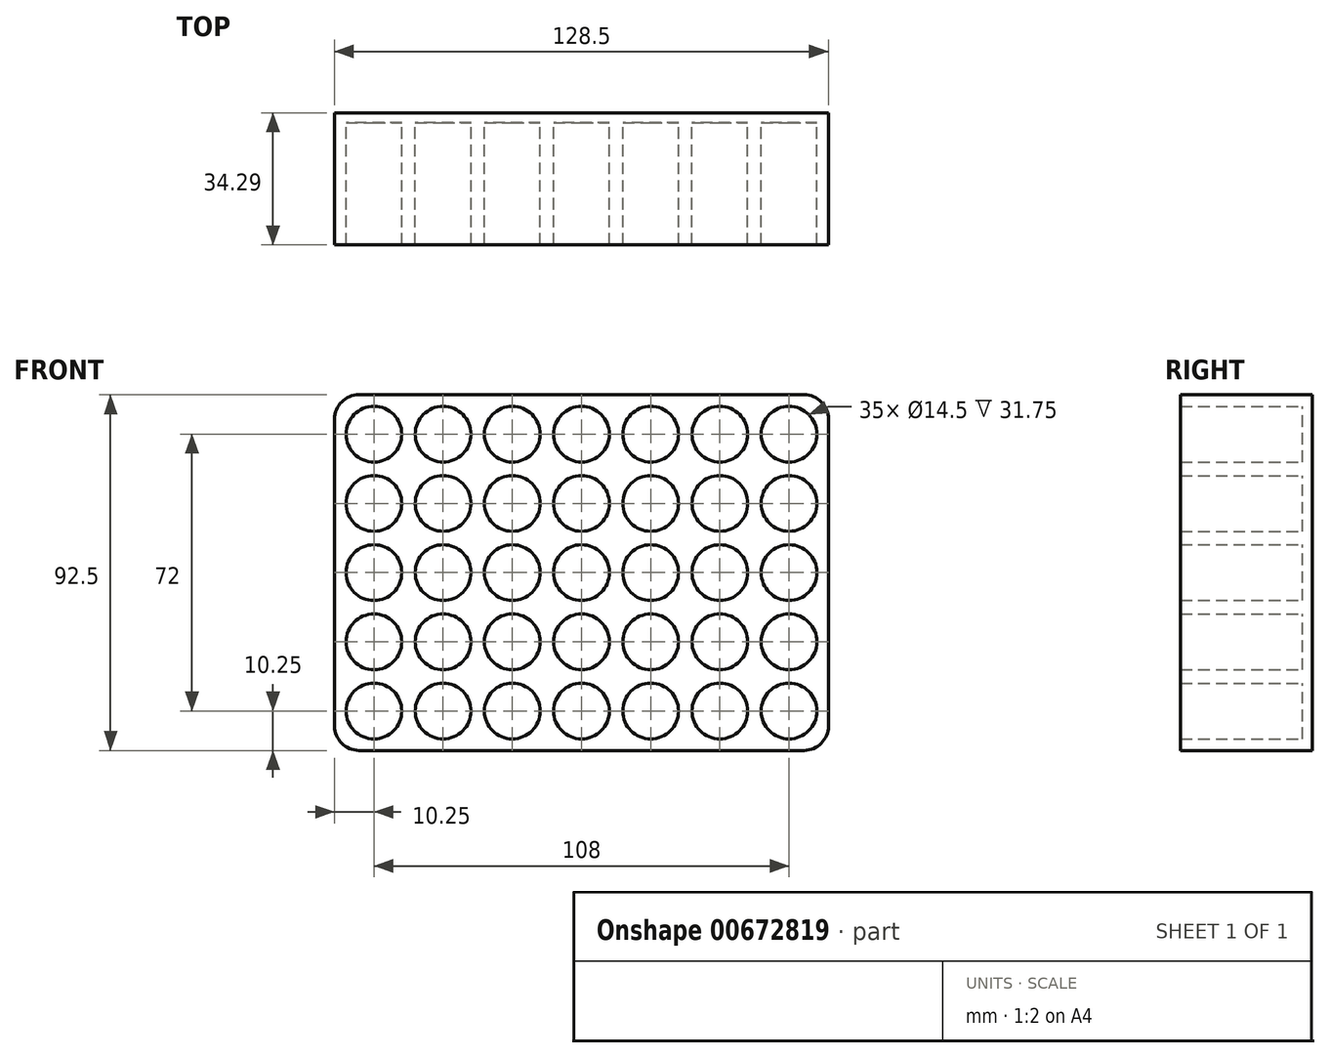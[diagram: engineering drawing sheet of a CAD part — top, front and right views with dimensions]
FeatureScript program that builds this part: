
annotation { "Feature Type Name" : "Feature", "Feature Type Description" : "" }
export const myFeature = defineFeature(function(context is Context, id is Id, definition is map)
    precondition{}
    {
        {
            var Q0;
            Q0=qCreatedBy(makeId("Front.planeOp"),FACE);
            var sketch = newSketch(context, id + "F0", { "sketchPlane" : qUnion([Q0])});
            skLineSegment(sketch, "E0.bottom", {"start": v(57.9, -46.25) * mm, "end": v(-57.9, -46.25) * mm});
            skLineSegment(sketch, "E0.top", {"start": v(57.9, 46.25) * mm, "end": v(-57.9, 46.25) * mm});
            skLineSegment(sketch, "E0.left", {"start": v(64.25, -39.9) * mm, "end": v(64.25, 39.9) * mm});
            skLineSegment(sketch, "E0.right", {"start": v(-64.25, -39.9) * mm, "end": v(-64.25, 39.9) * mm});
            skPoint(sketch, "E0.middle", {"position": v(0, 0) * mm});
            skCircle(sketch, "E1", {"center": v(0, 0) * mm, "radius": 7.25 * mm});
            skCircle(sketch, "E2.1.0.0", {"center": v(18, 0) * mm, "radius": 7.25 * mm});
            skCircle(sketch, "E2.2.0.0", {"center": v(36, 0) * mm, "radius": 7.25 * mm});
            skCircle(sketch, "E2.3.0.0", {"center": v(54, 0) * mm, "radius": 7.25 * mm});
            skLineSegment(sketch, "E2.direction1", {"start": v(0, 0) * mm, "end": v(18, 0) * mm, "construction": true});
            skCircle(sketch, "E3.1.0.0", {"center": v(-18, 0) * mm, "radius": 7.25 * mm});
            skCircle(sketch, "E3.2.0.0", {"center": v(-36, 0) * mm, "radius": 7.25 * mm});
            skCircle(sketch, "E3.3.0.0", {"center": v(-54, 0) * mm, "radius": 7.25 * mm});
            skLineSegment(sketch, "E3.direction1", {"start": v(0, 0) * mm, "end": v(-18, 0) * mm, "construction": true});
            skCircle(sketch, "E4", {"center": v(-54, 18) * mm, "radius": 7.25 * mm});
            skCircle(sketch, "E5", {"center": v(-54, -18) * mm, "radius": 7.25 * mm});
            skCircle(sketch, "E6", {"center": v(-36, -18) * mm, "radius": 7.25 * mm});
            skCircle(sketch, "E7", {"center": v(-36, 18) * mm, "radius": 7.25 * mm});
            skCircle(sketch, "E8", {"center": v(-18, 18) * mm, "radius": 7.25 * mm});
            skCircle(sketch, "E9", {"center": v(-18, -18) * mm, "radius": 7.25 * mm});
            skCircle(sketch, "E10", {"center": v(0, 18) * mm, "radius": 7.25 * mm});
            skCircle(sketch, "E11", {"center": v(0, -18) * mm, "radius": 7.25 * mm});
            skCircle(sketch, "E12", {"center": v(18, -18) * mm, "radius": 7.25 * mm});
            skCircle(sketch, "E13", {"center": v(36, -18) * mm, "radius": 7.25 * mm});
            skCircle(sketch, "E14", {"center": v(18, 18) * mm, "radius": 7.25 * mm});
            skCircle(sketch, "E15", {"center": v(36, 18) * mm, "radius": 7.25 * mm});
            skCircle(sketch, "E16", {"center": v(54, 18) * mm, "radius": 7.25 * mm});
            skCircle(sketch, "E17", {"center": v(54, -18) * mm, "radius": 7.25 * mm});
            skCircle(sketch, "E18", {"center": v(-54, -36) * mm, "radius": 7.25 * mm});
            skCircle(sketch, "E19", {"center": v(-36, -36) * mm, "radius": 7.25 * mm});
            skCircle(sketch, "E20", {"center": v(-18, -36) * mm, "radius": 7.25 * mm});
            skCircle(sketch, "E21", {"center": v(0, -36) * mm, "radius": 7.25 * mm});
            skCircle(sketch, "E22", {"center": v(18, -36) * mm, "radius": 7.25 * mm});
            skCircle(sketch, "E23", {"center": v(36, -36) * mm, "radius": 7.25 * mm});
            skCircle(sketch, "E24", {"center": v(54, -36) * mm, "radius": 7.25 * mm});
            skCircle(sketch, "E25", {"center": v(-54, 36) * mm, "radius": 7.25 * mm});
            skCircle(sketch, "E26", {"center": v(-36, 36) * mm, "radius": 7.25 * mm});
            skCircle(sketch, "E27", {"center": v(-18, 36) * mm, "radius": 7.25 * mm});
            skCircle(sketch, "E28", {"center": v(0, 36) * mm, "radius": 7.25 * mm});
            skCircle(sketch, "E29", {"center": v(18, 36) * mm, "radius": 7.25 * mm});
            skCircle(sketch, "E30", {"center": v(36, 36) * mm, "radius": 7.25 * mm});
            skCircle(sketch, "E31", {"center": v(54, 36) * mm, "radius": 7.25 * mm});
            skLineSegment(sketch, "E32", {"start": v(-54, 36) * mm, "end": v(-54, 18) * mm, "construction": true});
            skLineSegment(sketch, "E33", {"start": v(-54, 18) * mm, "end": v(-54, 0) * mm, "construction": true});
            skLineSegment(sketch, "E34", {"start": v(-54, 0) * mm, "end": v(-54, -18) * mm, "construction": true});
            skLineSegment(sketch, "E35", {"start": v(-54, -18) * mm, "end": v(-54, -36) * mm, "construction": true});
            skPoint(sketch, "E36.visualSharp", {"position": v(64.25, 46.25) * mm});
            skArc(sketch, "E36.filletArc", {"start": v(64.25, 39.9) * mm, "mid": v(62.4, 44.4) * mm, "end": v(57.9, 46.25) * mm});
            skPoint(sketch, "E37.visualSharp", {"position": v(64.25, -46.25) * mm});
            skArc(sketch, "E37.filletArc", {"start": v(57.9, -46.25) * mm, "mid": v(62.4, -44.4) * mm, "end": v(64.25, -39.9) * mm});
            skPoint(sketch, "E38.visualSharp", {"position": v(-64.25, -46.25) * mm});
            skArc(sketch, "E38.filletArc", {"start": v(-64.25, -39.9) * mm, "mid": v(-62.4, -44.4) * mm, "end": v(-57.9, -46.25) * mm});
            skPoint(sketch, "E39.visualSharp", {"position": v(-64.25, 46.25) * mm});
            skArc(sketch, "E39.filletArc", {"start": v(-57.9, 46.25) * mm, "mid": v(-62.4, 44.4) * mm, "end": v(-64.25, 39.9) * mm});
            skSolve(sketch);
        }
        {
            var Q0;
            Q0 = qSketchRegion(id + "F0", true);
            extrude(context, id + "F1", {"entities" : qUnion([Q0]), "depth" : 31.75 * mm, "offsetDistance" : 25.4 * mm});
        }
        {
            var Q0;
            Q0=makeQuery(id+"F1.opExtrude","CAP_FACE",FACE,{"disambiguationData":[OSD([sQuery(id+"F0.wireOp",EDGE,"E0.bottom"),sQuery(id+"F0.wireOp",EDGE,"E0.top"),sQuery(id+"F0.wireOp",EDGE,"E0.left"),sQuery(id+"F0.wireOp",EDGE,"E0.right"),sQuery(id+"F0.wireOp",EDGE,"E1"),sQuery(id+"F0.wireOp",EDGE,"E2.1.0.0"),sQuery(id+"F0.wireOp",EDGE,"E2.2.0.0"),sQuery(id+"F0.wireOp",EDGE,"E2.3.0.0"),sQuery(id+"F0.wireOp",EDGE,"E3.1.0.0"),sQuery(id+"F0.wireOp",EDGE,"E3.2.0.0"),sQuery(id+"F0.wireOp",EDGE,"E3.3.0.0"),sQuery(id+"F0.wireOp",EDGE,"E4"),sQuery(id+"F0.wireOp",EDGE,"E5"),sQuery(id+"F0.wireOp",EDGE,"E6"),sQuery(id+"F0.wireOp",EDGE,"E7"),sQuery(id+"F0.wireOp",EDGE,"E8"),sQuery(id+"F0.wireOp",EDGE,"E9"),sQuery(id+"F0.wireOp",EDGE,"E10"),sQuery(id+"F0.wireOp",EDGE,"E11"),sQuery(id+"F0.wireOp",EDGE,"E12"),sQuery(id+"F0.wireOp",EDGE,"E13"),sQuery(id+"F0.wireOp",EDGE,"E14"),sQuery(id+"F0.wireOp",EDGE,"E15"),sQuery(id+"F0.wireOp",EDGE,"E16"),sQuery(id+"F0.wireOp",EDGE,"E17"),sQuery(id+"F0.wireOp",EDGE,"E18"),sQuery(id+"F0.wireOp",EDGE,"E19"),sQuery(id+"F0.wireOp",EDGE,"E20"),sQuery(id+"F0.wireOp",EDGE,"E21"),sQuery(id+"F0.wireOp",EDGE,"E22"),sQuery(id+"F0.wireOp",EDGE,"E23"),sQuery(id+"F0.wireOp",EDGE,"E24"),sQuery(id+"F0.wireOp",EDGE,"E25"),sQuery(id+"F0.wireOp",EDGE,"E26"),sQuery(id+"F0.wireOp",EDGE,"E27"),sQuery(id+"F0.wireOp",EDGE,"E28"),sQuery(id+"F0.wireOp",EDGE,"E29"),sQuery(id+"F0.wireOp",EDGE,"E30"),sQuery(id+"F0.wireOp",EDGE,"E31"),sQuery(id+"F0.wireOp",EDGE,"E36.filletArc"),sQuery(id+"F0.wireOp",EDGE,"E37.filletArc"),sQuery(id+"F0.wireOp",EDGE,"E38.filletArc"),sQuery(id+"F0.wireOp",EDGE,"E39.filletArc")])],"isStart":true});
            var sketch = newSketch(context, id + "F2", { "sketchPlane" : qUnion([Q0])});
            skLineSegment(sketch, "E40.0", {"start": v(-57.9, -46.25) * mm, "end": v(57.9, -46.25) * mm});
            skArc(sketch, "E40.1", {"start": v(64.25, -39.9) * mm, "mid": v(62.4, -44.4) * mm, "end": v(57.9, -46.25) * mm});
            skLineSegment(sketch, "E40.2", {"start": v(64.25, -39.9) * mm, "end": v(64.25, 39.9) * mm});
            skArc(sketch, "E40.3", {"start": v(57.9, 46.25) * mm, "mid": v(62.4, 44.4) * mm, "end": v(64.25, 39.9) * mm});
            skLineSegment(sketch, "E40.4", {"start": v(-57.9, 46.25) * mm, "end": v(57.9, 46.25) * mm});
            skArc(sketch, "E40.5", {"start": v(-64.25, 39.9) * mm, "mid": v(-62.4, 44.4) * mm, "end": v(-57.9, 46.25) * mm});
            skLineSegment(sketch, "E40.6", {"start": v(-64.25, -39.9) * mm, "end": v(-64.25, 39.9) * mm});
            skArc(sketch, "E40.7", {"start": v(-57.9, -46.25) * mm, "mid": v(-62.4, -44.4) * mm, "end": v(-64.25, -39.9) * mm});
            skSolve(sketch);
        }
        {
            var Q0;
            Q0 = qSketchRegion(id + "F2", true);
            extrude(context, id + "F3", {"entities" : qUnion([Q0]), "operationType" : NewBodyOperationType.ADD, "depth" : 2.54 * mm, "offsetDistance" : 25.4 * mm});
        }
    });
